# Revit family: PGR_Noken_ShwrFitngsPckge_City
name_source: partatom
category: Plumbing Fixtures
revit_build: Autodesk Revit 2017 (Build: 20171027_0315(x64)
units: mm (PartAtom-declared; Revit-internal decimal feet)

## family parameters
Always vertical = Yes
Cut with Voids When Loaded = No
Host = Wall
OmniClass Number = 23.45.05.14.17
OmniClass Title = Showers
Part Type = Normal
Room Calculation Point = No
Round Connector Dimension = Use Diameter
Shared = Yes

## types (1)
- City-100190693
    AccessibilityPerformance = See ProductInformation for technical PDF
    AssetType = Fixed
    BIMObjectName = PGR_Noken_ShowerFittingsPackage_City_Chrome-650x140x72mm-100190693
    Category = Pr_40_20_87_75: Shower fittings package
    CodePerformance = EN 1112, EN 248, EN 1111, EN 1113
    Collection = City
    Color = Chrome
    Constituents = Shower pack
    DiameterCW = 0 mm
    DiameterHW = 0 mm
    DrainSize = 0 mm
    DurationUnit = Year
    Features = See ProductInformation for technical PDF
    Finish = Chrome
    FlowPressure = 0.0
    HasTray = No
    Height = 1200 mm
    IfcExportAs = IfcSanitaryTerminalType
    IfcExportType = Shower
    ManufacturerURL = www.noken.com
    Material = Brass
    MaterialMetal = PGR_Noken_Brass_Chrome
    MaterialThickness = 0 mm  [stored 0 ft]
    Model = 100190693
    ModelNumber = 100190693
    ModelReference = PACK DE DUCHA CITY CROMO
    NBSDescription = Shower fittings package
    NBSReference = 45-35-70/330
    Name = ShowerFittingsPackage_City_Chrome-650x140x72mm-100190693
    NettWeight = 1.2
    NominalDepth = 72 mm  [stored 0.23622 ft]
    NominalHeight = 72 mm  [stored 0.23622 ft]
    NominalLength = 650 mm  [stored 2.13255 ft]
    NominalWidth = 140 mm  [stored 0.459318 ft]
    ProductInformation = http://calidad.info-grupo.com:8081
    Reference = -
    ShowerHeadDescription = City N showe pack. Includes handshower bar with bracket, 1-function 100191064 - N770000228 handshower and flexi shower hose PVC coated twist free 100137848 - N199999490. Material brass, fiinish chrome plated,
 dimension 650x72 mm, net product weithg 1,2 kg. 5 years warranty for superficial finishes and 2 years for the rest of components. EN 1111, EN 1112, EN 248
    ShowerType = UNSET
    Size = 650x140x72
    Status = UNSET
    SustainabilityPerformance = See ProductInformation for technical PDF
    TechnicalDrawing = See ProductInformation for technical PDF
    Type Image = 100190693.jpg
    URL = www.noken.com
    Uniclass2015Code = Pr_40_20_87_75
    Uniclass2015Title = Shower fittings package
    Uniclass2015Version = V1_9
    Version = 1
    WarrantyDescription = See ProductInformation for technical PDF
    WarrantyDurationUnit = Year

note: source unit labels omitted for FlowPressure — the stored unit's dimension contradicts the parameter name (converter mislabeling)

note: [stored X ft] marks values corroborated as IEEE doubles in the binary element streams (Revit-internal decimal feet)

## geometry (parser evidence)
native form markers: Blend x2, Sweep x5
no freeform markers — native parametric forms only
